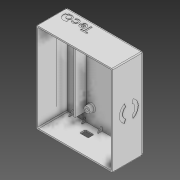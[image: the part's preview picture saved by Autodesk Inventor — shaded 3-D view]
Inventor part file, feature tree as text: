
AUTODESK INVENTOR PART (.ipt)
format: ipt  version: 2021 (Build 250183000, 183)  size: 400,384 bytes
history: native  units: mm
features: sketch x8, extrude x8, fillet x5, plane x4, other x2, mirror x2
ambient origin geometry x8: Origin, YZ Plane, XZ Plane, XY Plane, X Axis, Y Axis, Z Axis, Center Point
bodies: Body1 (feature_tree)
feature tree (29):
  other  "Sólido1"
  sketch  "Boceto1"  dims[d0=74.8mm d1=89.4mm]
  extrude  "Extrusión1"  Depth=89.4mm
  extrude  "Extrusión2"  Depth=1.5mm
  fillet  "Empalme1"  Radius=1.6mm
  extrude  "Extrusión3"  Depth=1.0mm
  fillet  "Empalme2"  Radius=1.0mm
  extrude  "Extrusión5"  Depth=2.8mm
  extrude  "Extrusión6"  Depth=22.037mm
  extrude  "Extrusión7"  Depth=2.8mm
  plane  "Plano de trabajo2"
  other  "Nervio1"
  fillet  "Empalme3"  Radius=2.8mm
  plane  "Plano de trabajo3"
  mirror  "Simetría1"
  extrude  "Extrusión8"  Depth=16.552mm
  extrude  "Extrusión9"  Depth=2.8mm
  plane  "Plano de trabajo4"
  mirror  "Simetría2"
  fillet  "Empalme4"  Radius=5.0mm
  fillet  "Empalme5"  Radius=17.767mm
  sketch  "Boceto2"  dims[d2=1.5mm d3=1.5mm d4=1.6mm d5=0.0mm]
  sketch  "Boceto4"  dims[d6=32.8mm d7=0.0mm d8=1.0mm d9=1.0mm]
  sketch  "Boceto5"  dims[d10=68.5mm d11=2.8mm]
  sketch  "Boceto6"  dims[d12=6.5mm d13=22.037mm]
  plane  "Plano de trabajo1"
  sketch  "Boceto7"  dims[d14=41.139mm d15=2.8mm d16=6.5mm d17=28.717mm d18=2.8mm]
  sketch  "Boceto9"  dims[d19=6.5mm d20=16.552mm]
  sketch  "Boceto10"  dims[d21=25.894mm d22=2.8mm d23=5.0mm d24=17.767mm d25=75.241mm d26=5.0mm d27=0.0mm d32=1.0mm d33=80.0mm d34=0.0mm d35=80.0mm d36=0.0mm d37=1.5mm d38=1.5mm d39=1.5mm d40=1.5mm d41=4.6mm d42=4.6mm d43=0.5mm d44=1.5mm d45=0.0mm d46=45.0deg d47=3.0mm d48=1.0mm d49=1.0mm d50=0.0mm d51=0.0mm d52=1.0mm d53=1.0mm d54=1.0mm d55=4.764661mm d56=4.667598mm d57=7.395626mm d58=0.35mm d59=0.0mm d60=1.5mm d61=1.5mm d62=1.5mm d63=1.5mm d64=0.35mm d65=0.0mm d66=1.0mm d67=2.0mm]
